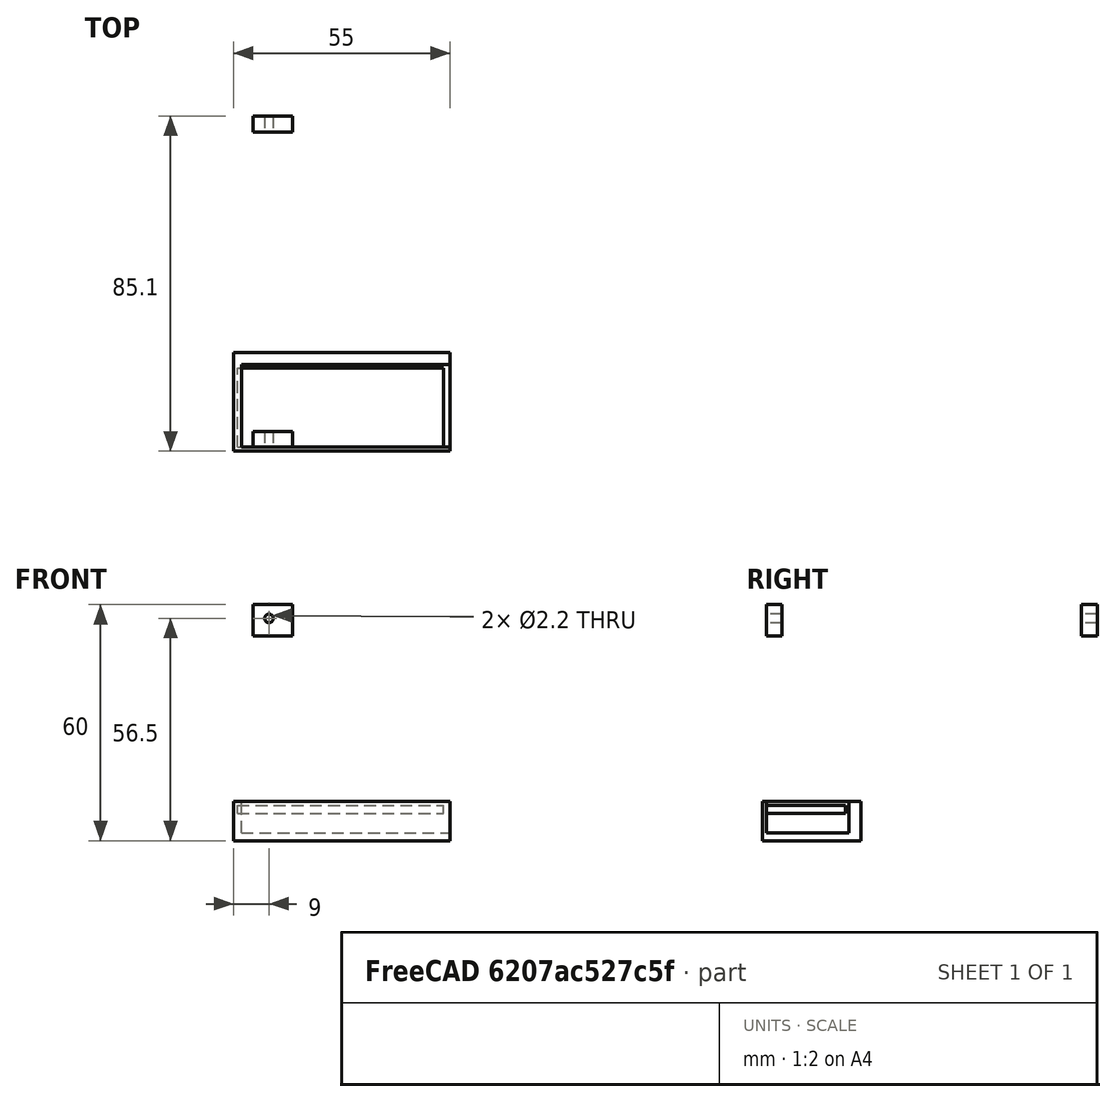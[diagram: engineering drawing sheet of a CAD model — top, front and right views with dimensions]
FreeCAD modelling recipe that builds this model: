
FCSTD DOCUMENT  (FreeCAD 0.18.4R)
Label: rasbpi3
License: All rights reserved
LicenseURL: http://en.wikipedia.org/wiki/All_rights_reserved
objects: Part::Box×5, App::Part×4, Mesh::Feature×3, Part::Cut×3, Part::Feature×3, Part::Compound×1, Part::Cylinder×1, Part::FeaturePython×1
note: 14 computed .brp shape members not serialized (recipe doc carries the construction recipe); baked Part::Feature solids carry a one-line shape summary decoded from their .brp

FEATURE [Mesh::Feature] RASPBERRY_PI_4B_v7
  Placement = pos=(0,1.6e-15,7) rot=(0,0.707107,0.707107;3.14159rad)
FEATURE [Mesh::Feature] Raspberry_Pi_Vertical_Case
FEATURE [Part::Box] Box  label="Cube"
  AttacherType = Attacher::AttachEngine3D
  Height = 2
  Length = 52.35
  Placement = pos=(-8,-53,6) rot=(0,0,1;0rad)
  Width = 20.16
FEATURE [Part::Box] Box001  label="Cube001"
  AttacherType = Attacher::AttachEngine3D
  Height = 10
  Length = 55
  Placement = pos=(-9,-54,0) rot=(0,0,1;0rad)
  Width = 25
FEATURE [Part::Box] Box002  label="Cube002"
  AttacherType = Attacher::AttachEngine3D
  Height = 8
  Length = 53
  Placement = pos=(-7,-53,2) rot=(0,0,1;0rad)
  Width = 21
FEATURE [Part::Cut] Cut
  Base = -> Box001
  Placement = pos=(0,0,-1) rot=(0,0,1;0rad)
  Tool = -> Box002
FEATURE [App::Part] Part  label="pu box"
  Origin = -> Origin
FEATURE [Part::Box] Box003  label="Cube003"
  AttacherType = Attacher::AttachEngine3D
  Height = 10
  Length = 55
  Placement = pos=(-11,-53,0) rot=(0,0,1;0rad)
  Width = 25
FEATURE [Part::Feature] Raspberry_Pi_Vertical_Case001
  shape: bbox 95.6 x 109.2 x 26 mm, 4754 faces, 0 solids (baked)
FEATURE [Part::Cut] Cut001
  Base = -> Raspberry_Pi_Vertical_Case001
  Tool = -> Box003
FEATURE [App::Part] Part001  label="box"
  Group = -> [Box003,Raspberry_Pi_Vertical_Case001,Cut001]
  Origin = -> Origin001
FEATURE [Part::Feature] Cut001001  label="Cut002"
  shape: bbox 95.6 x 109.2 x 26 mm, 2336 faces, 0 solids (baked)
FEATURE [Part::Compound] Compound  label="final bottom"
  Links = -> [Cut001001,Cut]
FEATURE [Mesh::Feature] Raspberry_Pi_Case_Lid
  Placement = pos=(-99,89,61) rot=(1,0,0;3.14159rad)
FEATURE [Part::Cylinder] Cylinder
  Angle = 360
  AttacherType = Attacher::AttachEngine3D
  Height = 120
  Placement = pos=(0,50,55.5) rot=(1,0,0;1.5708rad)
  Radius = 1.1
FEATURE [Part::Feature] Raspberry_Pi_Case_Lid001
  shape: bbox 92.2 x 89.2 x 17 mm, 2374 faces, 0 solids (baked)
FEATURE [Part::Box] Box004  label="Cube004"
  AttacherType = Attacher::AttachEngine3D
  Height = 8
  Length = 10
  Placement = pos=(-4,-53,51) rot=(0,0,1;0rad)
  Width = 4
FEATURE [Part::FeaturePython] Array  # Draft array (typed FeaturePython)
  Angle = 360
  ArrayType = 0
  Axis = (0,0,1)
  Base = -> Box004
  Center = (0,0,0)
  Fuse = false
  IntervalAxis = (0,0,0)
  IntervalX = (1,0,0)
  IntervalY = (0,80.1,0)
  IntervalZ = (0,0,1)
  NumberPolar = 1
  NumberX = 1
  NumberY = 2
  NumberZ = 1
FEATURE [Part::Cut] Cut001002
  Base = -> Array
  Tool = -> Cylinder
FEATURE [App::Part] Part002  label="final lid"
  Group = -> [Raspberry_Pi_Case_Lid001,Box004,Cylinder,Array,Cut001002]
  Origin = -> Origin002
FEATURE [App::Part] Part003  label="final bottom001"
  Group = -> [Box002,Cut001001,Box001,Cut,Compound]
  Origin = -> Origin003
